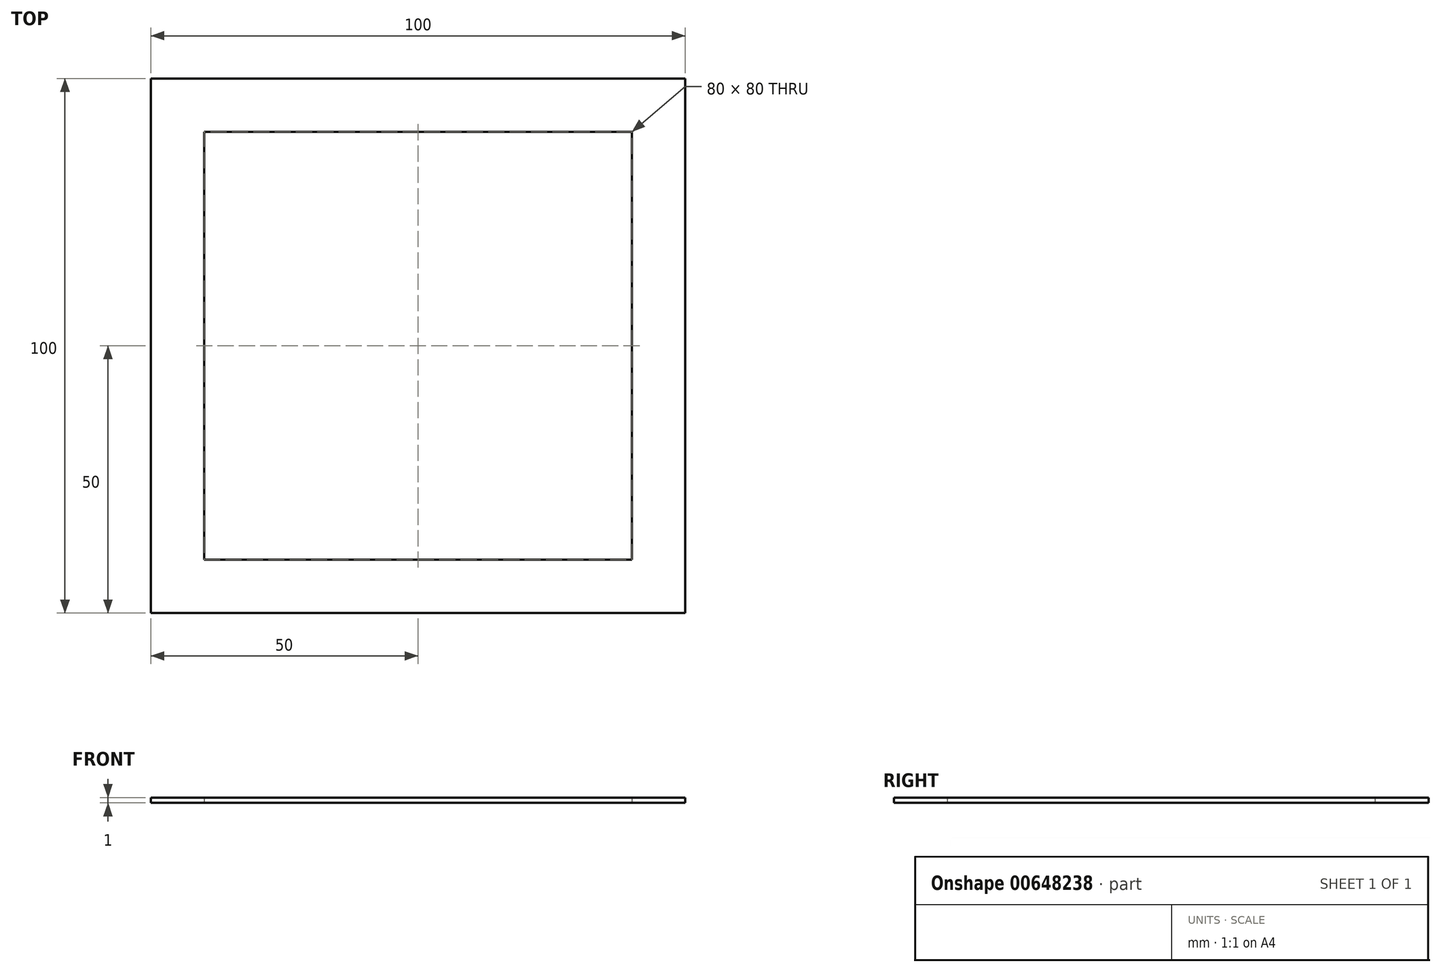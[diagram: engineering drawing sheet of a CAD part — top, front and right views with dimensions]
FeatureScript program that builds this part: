
annotation { "Feature Type Name" : "Feature", "Feature Type Description" : "" }
export const myFeature = defineFeature(function(context is Context, id is Id, definition is map)
    precondition{}
    {
        {
            var Q0;
            Q0=qCreatedBy(makeId("Top.planeOp"),FACE);
            var sketch = newSketch(context, id + "F0", { "sketchPlane" : qUnion([Q0])});
            skLineSegment(sketch, "E0.bottom", {"start": v(0, 0) * mm, "end": v(100, 0) * mm});
            skLineSegment(sketch, "E0.top", {"start": v(0, 100) * mm, "end": v(100, 100) * mm});
            skLineSegment(sketch, "E0.left", {"start": v(0, 0) * mm, "end": v(0, 100) * mm});
            skLineSegment(sketch, "E0.right", {"start": v(100, 0) * mm, "end": v(100, 100) * mm});
            skLineSegment(sketch, "E1.bottom", {"start": v(10, 10) * mm, "end": v(90, 10) * mm});
            skLineSegment(sketch, "E1.top", {"start": v(10, 90) * mm, "end": v(90, 90) * mm});
            skLineSegment(sketch, "E1.left", {"start": v(10, 10) * mm, "end": v(10, 90) * mm});
            skLineSegment(sketch, "E1.right", {"start": v(90, 10) * mm, "end": v(90, 90) * mm});
            skSolve(sketch);
        }
        {
            var Q0;
            Q0=makeQuery(id+"F0.imprint","IMPRINT",FACE,{"disambiguationData":[TD([[makeQuery(id+"F0.imprint","IMPRINT",EDGE,{"derivedFrom":sQuery(id+"F0.wireOp",EDGE,"E0.bottom")}),1.0]])]});
            extrude(context, id + "F1", {"entities" : qUnion([Q0]), "depth" : 1 * mm, "offsetDistance" : 25 * mm});
        }
    });
